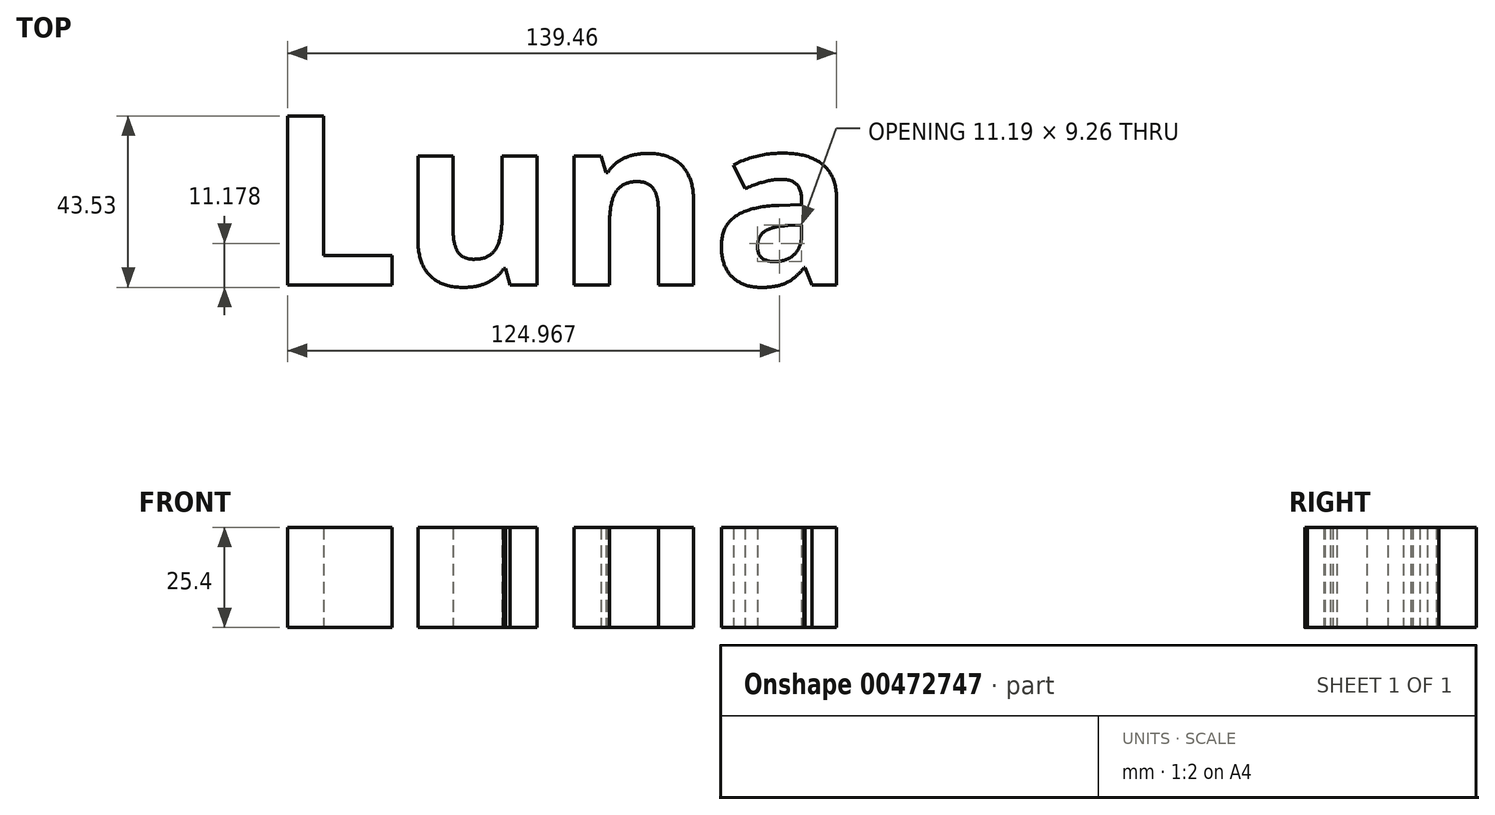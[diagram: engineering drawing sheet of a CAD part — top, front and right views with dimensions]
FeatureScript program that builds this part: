
annotation { "Feature Type Name" : "Feature", "Feature Type Description" : "" }
export const myFeature = defineFeature(function(context is Context, id is Id, definition is map)
    precondition{}
    {
        {
            var Q0;
            Q0=qCreatedBy(makeId("Top.planeOp"),FACE);
            var sketch = newSketch(context, id + "F0", { "sketchPlane" : qUnion([Q0])});
            skText(sketch, "E0", { "text": "Luna\n", "fontName": "OpenSans-Bold.ttf"});
            const initialGuessF0  = {"E0": [-0.0769, -0.02174, 1, 0, 0.04331]};
            skSetInitialGuess(sketch, initialGuessF0);
            skSolve(sketch);
        }
        {
            var Q0;
            Q0 = qSketchRegion(id + "F0", true);
            extrude(context, id + "F1", {"entities" : qUnion([Q0]), "depth" : 25.4 * mm});
        }
    });
